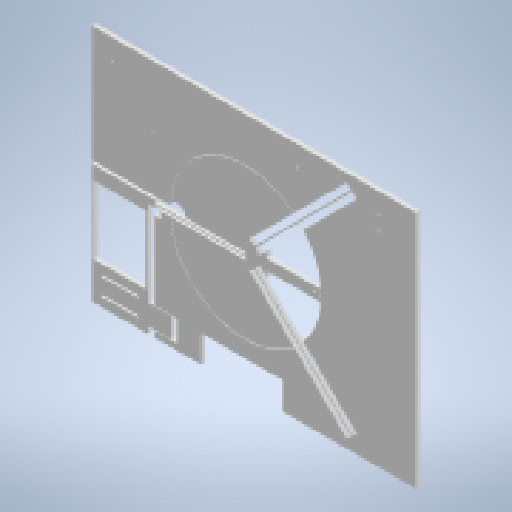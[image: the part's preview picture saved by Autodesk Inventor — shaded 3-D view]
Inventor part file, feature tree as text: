
AUTODESK INVENTOR PART (.ipt)
format: ipt  version: 2023 (Build 270158000, 158)  size: 497,664 bytes
history: native  units: mm
features: extrude x8, sketch x8, reference x5, other x4, projected_geometry x1
ambient origin geometry x8: Origin, YZ Plane, XZ Plane, XY Plane, X Axis, Y Axis, Z Axis, Center Point
bodies: Solid1 (feature_tree)
feature tree (26):
  other  "<userpath>\OneDrive\ClawdDrive\Objet3D\IminaProbe\RoueMDF\Settings.xlsx"
  extrude  "Extrusion1"  Depth=400.0mm
  extrude  "Extrusion2"  TaperAngle=0.0deg  [1 undecoded]
  extrude  "Extrusion3"  Depth=175.0mm
  extrude  "Extrusion4"  Depth=40.0mm
  extrude  "Extrusion5"  Depth=10.0mm
  extrude  "Extrusion6"  Depth=10.0mm
  extrude  "Extrusion7"  Depth=1.0mm
  extrude  "Extrusion8"  Depth=1.0mm
  sketch  "Sketch1"  dims[d0=350.0mm d1=400.0mm]
  sketch  "Sketch2"  dims[d2=6.0mm d3=0.0mm]
  reference  "Reference1"
  sketch  "Sketch3"  dims[d4=175.0mm d5=175.0mm]
  sketch  "Sketch4"  dims[d6=220.0mm d7=40.0mm]
  sketch  "Sketch5"  dims[d8=10.0mm d9=10.0mm]
  projected_geometry  "Projected Loop1"
  sketch  "Sketch6"  dims[d10=10.0mm d11=10.0mm]
  sketch  "Sketch7"  dims[d12=1.0mm d13=1.0mm]
  sketch  "Sketch8"  dims[d14=1.0mm d15=1.0mm d16=200.0mm d17=200.0mm d18=222.0mm d19=100.0mm d20=2.25mm d21=2.25mm d22=10.0mm d24=20.0mm d25=0.0mm d26=6.0mm d27=4.0mm d28=4.0mm d29=20.0mm d30=0.0mm d31=1.0mm d32=1.0mm d33=10.0mm d34=30.0mm d35=10.0mm d36=100.0mm d37=0.0mm d38=3.0mm d39=6.0mm d40=0.0mm d41=25.0mm d42=40.0mm d43=120.0mm d44=120.0mm d45=6.0mm d46=0.0mm d47=3.0mm d48=30.0mm d49=30.0mm d50=90.0mm d51=90.0mm d52=3.0mm d53=3.0mm d54=100.0mm d55=30.0mm d56=6.0mm d57=0.0mm d61=8.0mm d62=8.0mm d63=10.0mm d64=0.0mm d65=15.0mm d66=15.0mm d67=15.0mm d68=15.0mm d69=15.0mm d70=15.0mm d71=15.0mm d72=15.0mm d73=3.0mm d74=3.0mm d75=3.0mm d76=3.0mm d77=52.128569mm d78=10.0mm d79=0.0mm d80=25.0mm d81=475.0mm d82=6.0mm d83=0.0mm d84=3.0mm d85=3.0mm d86=15.0mm d87=15.0mm d88=6.0mm d89=0.0mm]
  reference  "Reference2"
  reference  "Reference3"
  reference  "Reference4"
  reference  "Reference5"
  other  "<userpath>\OneDrive\ClawdDrive\Objet3D\IminaProbe\RoueMDF\Assembly1.iam"
  other  "Assembly1.iam"
  other  "Inverter:1"
note: 1 required parameter value undecoded (feature->parameter linkage not recoverable at this tier; creation-order binding heuristic only, values carry confidence <= 0.55)
